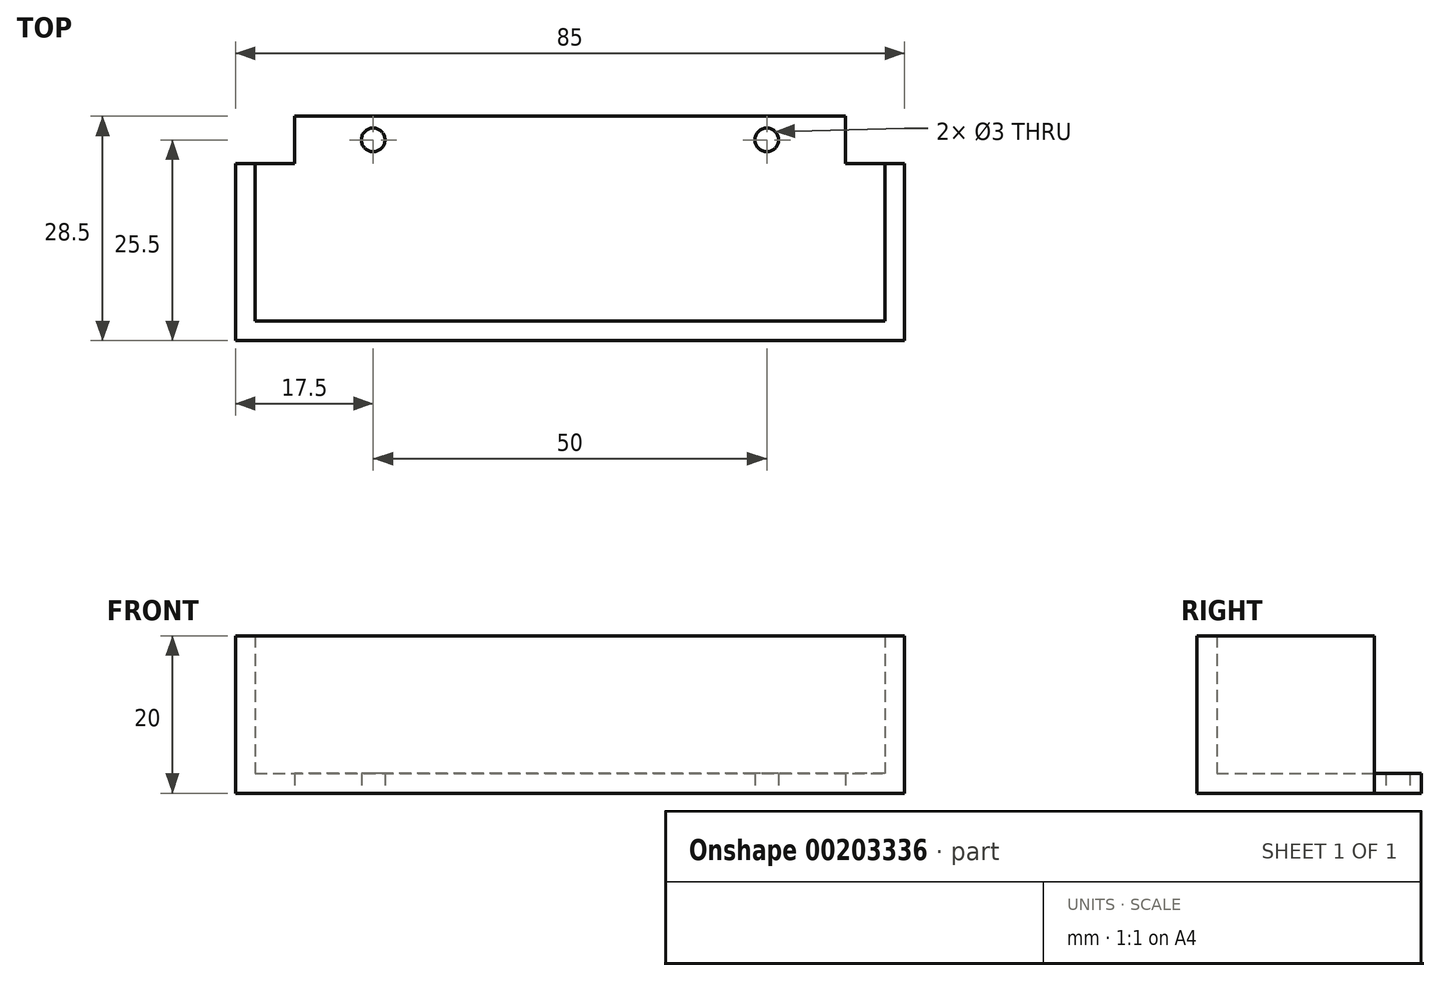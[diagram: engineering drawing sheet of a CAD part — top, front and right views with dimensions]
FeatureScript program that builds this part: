
annotation { "Feature Type Name" : "Feature", "Feature Type Description" : "" }
export const myFeature = defineFeature(function(context is Context, id is Id, definition is map)
    precondition{}
    {
        {
            var Q0;
            Q0=qCreatedBy(makeId("Top.planeOp"),FACE);
            var sketch = newSketch(context, id + "F0", { "sketchPlane" : qUnion([Q0])});
            skLineSegment(sketch, "E0.top", {"start": v(35, 3) * mm, "end": v(-35, 3) * mm});
            skLineSegment(sketch, "E0.left", {"start": v(35, -3) * mm, "end": v(35, 3) * mm});
            skLineSegment(sketch, "E0.right", {"start": v(-35, -3) * mm, "end": v(-35, 3) * mm});
            skPoint(sketch, "E0.middle", {"position": v(0, 0) * mm});
            skLineSegment(sketch, "E1", {"start": v(-35, -3) * mm, "end": v(-35, -23) * mm});
            skLineSegment(sketch, "E2", {"start": v(-35, -23) * mm, "end": v(35, -23) * mm});
            skLineSegment(sketch, "E3", {"start": v(35, -23) * mm, "end": v(35, -3) * mm});
            skSolve(sketch);
        }
        {
            var Q0;
            Q0 = qSketchRegion(id + "F0", true);
            extrude(context, id + "F1", {"entities" : qUnion([Q0]), "depth" : 2.5 * mm});
        }
        {
            var Q0;
            Q0=makeQuery(id+"F1.opExtrude","CAP_FACE",FACE,{"disambiguationData":[OSD([sQuery(id+"F0.wireOp",EDGE,"E0.bottom"),sQuery(id+"F0.wireOp",EDGE,"E0.top"),sQuery(id+"F0.wireOp",EDGE,"E0.left"),sQuery(id+"F0.wireOp",EDGE,"E0.right")])],"isStart":true});
            var sketch = newSketch(context, id + "F2", { "sketchPlane" : qUnion([Q0])});
            skCircle(sketch, "E4", {"center": v(-25, 0) * mm, "radius": 1.5 * mm});
            skLineSegment(sketch, "E5", {"start": v(-35, 0) * mm, "end": v(35, 0) * mm, "construction": true});
            skLineSegment(sketch, "E6", {"start": v(0, 23) * mm, "end": v(0, -3) * mm, "construction": true});
            skCircle(sketch, "E7.MirrorC", {"center": v(25, 0) * mm, "radius": 1.5 * mm});
            skSolve(sketch);
        }
        {
            var Q0;
            Q0 = qSketchRegion(id + "F2", true);
            extrude(context, id + "F3", {"entities" : qUnion([Q0]), "operationType" : NewBodyOperationType.REMOVE, "endBound" : BoundingType.THROUGH_ALL, "oppositeDirection" : true, "depth" : 25 * mm});
        }
        {
            var Q0;
            Q0=makeQuery(id+"F1.opExtrude","SWEPT_FACE",FACE,{"disambiguationData":[OSD([sQuery(id+"F0.wireOp",EDGE,"E0.right"),sQuery(id+"F0.wireOp",EDGE,"E1")])]});
            var sketch = newSketch(context, id + "F4", { "sketchPlane" : qUnion([Q0])});
            skLineSegment(sketch, "E8.bottom", {"start": v(23, 2.5) * mm, "end": v(3, 2.5) * mm});
            skLineSegment(sketch, "E8.top", {"start": v(23, 0) * mm, "end": v(3, 0) * mm});
            skLineSegment(sketch, "E8.left", {"start": v(23, 2.5) * mm, "end": v(23, 0) * mm});
            skLineSegment(sketch, "E8.right", {"start": v(3, 2.5) * mm, "end": v(3, 0) * mm});
            skSolve(sketch);
        }
        {
            var Q0;
            Q0 = qSketchRegion(id + "F4", true);
            extrude(context, id + "F5", {"entities" : qUnion([Q0]), "operationType" : NewBodyOperationType.ADD, "depth" : 5 * mm});
        }
        {
            var Q0;
            Q0=makeQuery(id+"F1.opExtrude","SWEPT_BODY",BODY,{"disambiguationData":[OSD([sQuery(id+"F0.wireOp",EDGE,"E0.top"),sQuery(id+"F0.wireOp",EDGE,"E0.left"),sQuery(id+"F0.wireOp",EDGE,"E0.right"),sQuery(id+"F0.wireOp",EDGE,"E1"),sQuery(id+"F0.wireOp",EDGE,"E2"),sQuery(id+"F0.wireOp",EDGE,"E3")])]});
            var Q1;
            Q1=qCreatedBy(makeId("Right.planeOp"),FACE);
            mirror(context, id + "F6", {"operationType" : NewBodyOperationType.ADD, "entities" : qUnion([Q0]), "mirrorPlane" : qUnion([Q1])});
        }
        {
            var Q0;
            {var subQ0=makeQuery(id+"F5.boolean.opBoolean","MERGE",FACE,{"derivedFrom":[makeQuery(id+"F1.opExtrude","SWEPT_FACE",FACE,{"disambiguationData":[OSD([sQuery(id+"F0.wireOp",EDGE,"E2")])]}),makeQuery(id+"F5.opExtrude","SWEPT_FACE",FACE,{"disambiguationData":[OSD([sQuery(id+"F4.wireOp",EDGE,"E8.left")])]})]});Q0=makeQuery(id+"F6.boolean.opBoolean","MERGE",FACE,{"derivedFrom":[subQ0,makeQuery(id+"F6.opPattern","COPY",FACE,{"derivedFrom":subQ0,"instanceName":"1"})]});}
            var sketch = newSketch(context, id + "F7", { "sketchPlane" : qUnion([Q0])});
            skLineSegment(sketch, "E9.bottom", {"start": v(-40, 0) * mm, "end": v(40, 0) * mm});
            skLineSegment(sketch, "E9.top", {"start": v(-40, 20) * mm, "end": v(40, 20) * mm});
            skLineSegment(sketch, "E9.left", {"start": v(-40, 0) * mm, "end": v(-40, 20) * mm});
            skLineSegment(sketch, "E9.right", {"start": v(40, 0) * mm, "end": v(40, 20) * mm});
            skSolve(sketch);
        }
        {
            var Q0;
            Q0 = qSketchRegion(id + "F7", true);
            extrude(context, id + "F8", {"entities" : qUnion([Q0]), "operationType" : NewBodyOperationType.ADD, "depth" : 2.5 * mm});
        }
        {
            var Q0;
            Q0=makeQuery(id+"F8.boolean.opBoolean","MERGE",FACE,{"derivedFrom":[makeQuery(id+"F6.opPattern","COPY",FACE,{"derivedFrom":makeQuery(id+"F5.opExtrude","CAP_FACE",FACE,{"disambiguationData":[OSD([sQuery(id+"F4.wireOp",EDGE,"E8.bottom"),sQuery(id+"F4.wireOp",EDGE,"E8.top"),sQuery(id+"F4.wireOp",EDGE,"E8.left"),sQuery(id+"F4.wireOp",EDGE,"E8.right")])],"isStart":false}),"instanceName":"1"}),makeQuery(id+"F8.opExtrude","SWEPT_FACE",FACE,{"disambiguationData":[OSD([sQuery(id+"F7.wireOp",EDGE,"E9.right")])]})]});
            var sketch = newSketch(context, id + "F9", { "sketchPlane" : qUnion([Q0])});
            skLineSegment(sketch, "E10.bottom", {"start": v(-25.5, 0) * mm, "end": v(-3, 0) * mm});
            skLineSegment(sketch, "E10.top", {"start": v(-25.5, 20) * mm, "end": v(-3, 20) * mm});
            skLineSegment(sketch, "E10.left", {"start": v(-25.5, 0) * mm, "end": v(-25.5, 20) * mm});
            skLineSegment(sketch, "E10.right", {"start": v(-3, 0) * mm, "end": v(-3, 20) * mm});
            skSolve(sketch);
        }
        {
            var Q0;
            Q0 = qSketchRegion(id + "F9", true);
            extrude(context, id + "F10", {"entities" : qUnion([Q0]), "operationType" : NewBodyOperationType.ADD, "depth" : 2.5 * mm});
        }
        {
            var Q0;
            Q0=makeQuery(id+"F1.opExtrude","SWEPT_BODY",BODY,{"disambiguationData":[OSD([sQuery(id+"F0.wireOp",EDGE,"E0.top"),sQuery(id+"F0.wireOp",EDGE,"E0.left"),sQuery(id+"F0.wireOp",EDGE,"E0.right"),sQuery(id+"F0.wireOp",EDGE,"E1"),sQuery(id+"F0.wireOp",EDGE,"E2"),sQuery(id+"F0.wireOp",EDGE,"E3")])]});
            var Q1;
            Q1=qCreatedBy(makeId("Right.planeOp"),FACE);
            mirror(context, id + "F11", {"operationType" : NewBodyOperationType.ADD, "entities" : qUnion([Q0]), "mirrorPlane" : qUnion([Q1])});
        }
    });
